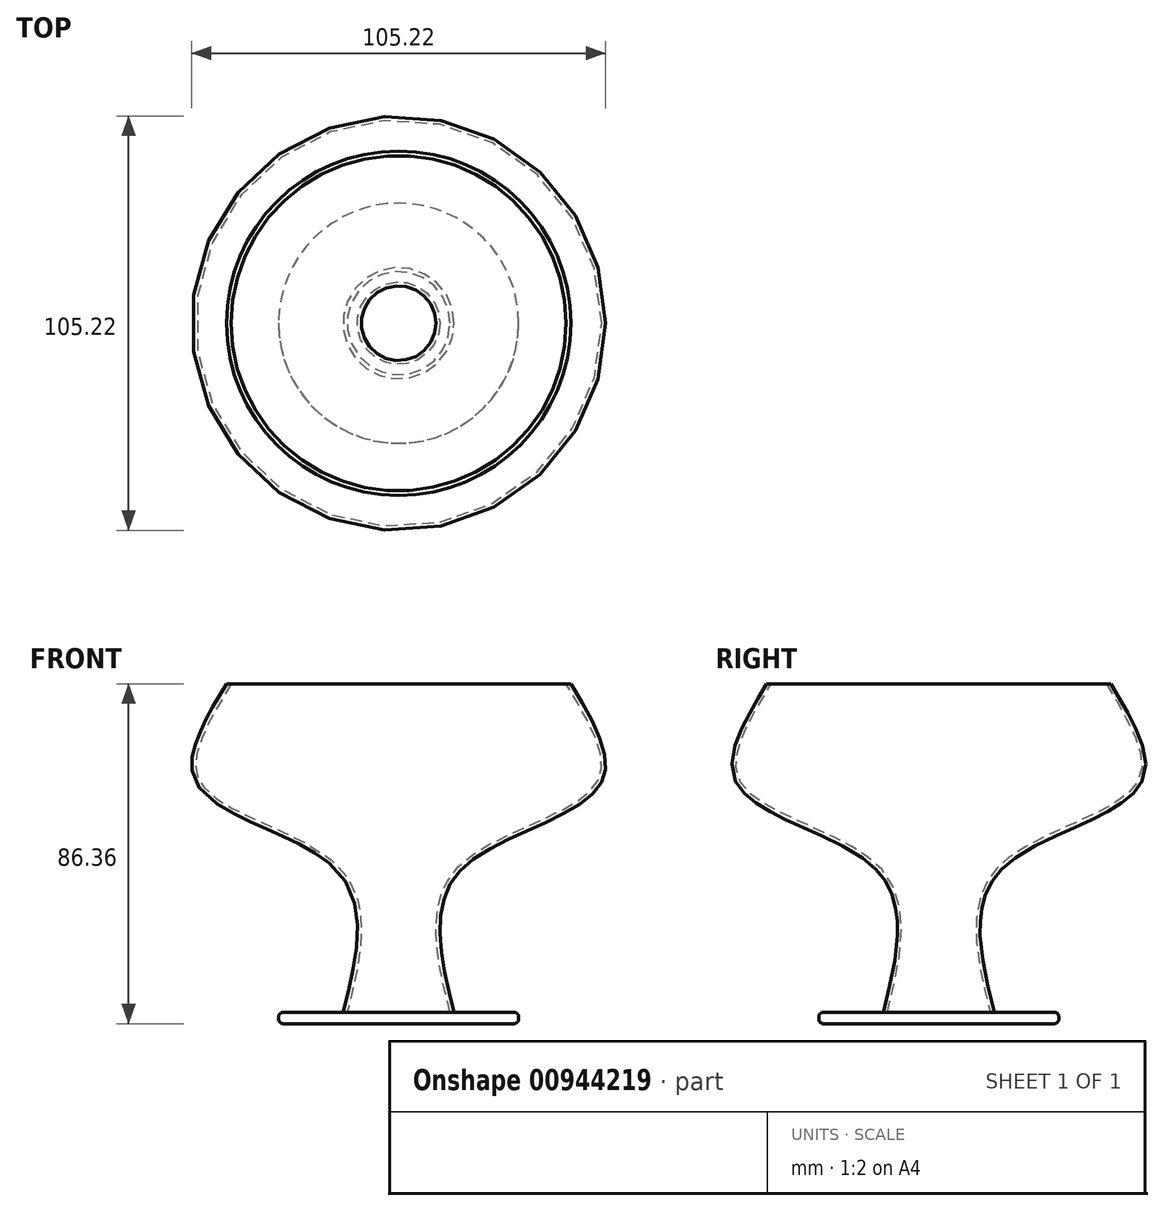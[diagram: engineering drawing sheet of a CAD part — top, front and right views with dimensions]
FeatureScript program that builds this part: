
annotation { "Feature Type Name" : "Feature", "Feature Type Description" : "" }
export const myFeature = defineFeature(function(context is Context, id is Id, definition is map)
    precondition{}
    {
        {
            var Q0;
            Q0=qCreatedBy(makeId("Top.planeOp"),FACE);
            var sketch = newSketch(context, id + "F0", { "sketchPlane" : qUnion([Q0])});
            skCircle(sketch, "E0", {"center": v(0, 0) * mm, "radius": 14.89 * mm});
            skSolve(sketch);
        }
        {
            var Q0;
            Q0=qCreatedBy(makeId("Top.planeOp"),FACE);
            cPlane(context, id + "F1", {"entities" : qUnion([Q0]), "cplaneType" : CPlaneType.OFFSET, "offset" : 86.36 * mm, "width" : 152.4 * mm, "height" : 152.4 * mm});
        }
        {
            var Q0;
            Q0=qCreatedBy(id+"F1.planeOp",FACE);
            var sketch = newSketch(context, id + "F2", { "sketchPlane" : qUnion([Q0])});
            skCircle(sketch, "E1", {"center": v(0, 0) * mm, "radius": 43.74 * mm});
            skSolve(sketch);
        }
        {
            var Q0;
            Q0=qCreatedBy(makeId("Top.planeOp"),FACE);
            cPlane(context, id + "F3", {"entities" : qUnion([Q0]), "cplaneType" : CPlaneType.OFFSET, "offset" : 38.2 * mm, "width" : 150 * mm, "height" : 150 * mm});
        }
        {
            var Q0;
            Q0=qCreatedBy(id+"F3.planeOp",FACE);
            cPlane(context, id + "F4", {"entities" : qUnion([Q0]), "cplaneType" : CPlaneType.OFFSET, "offset" : 25 * mm, "width" : 150 * mm, "height" : 150 * mm});
        }
        {
            var Q0;
            Q0=qCreatedBy(id+"F4.planeOp",FACE);
            var sketch = newSketch(context, id + "F5", { "sketchPlane" : qUnion([Q0])});
            skCircle(sketch, "E2", {"center": v(0, 0) * mm, "radius": 52.3 * mm});
            skSolve(sketch);
        }
        {
            var Q0;
            Q0=qCreatedBy(id+"F3.planeOp",FACE);
            var sketch = newSketch(context, id + "F6", { "sketchPlane" : qUnion([Q0])});
            skCircle(sketch, "E3", {"center": v(0, 0) * mm, "radius": 15 * mm});
            skSolve(sketch);
        }
        {
            var Q0;
            Q0=makeQuery(id+"F0.imprint","IMPRINT",FACE,{"disambiguationData":[TD([[makeQuery(id+"F0.imprint","IMPRINT",EDGE,{"derivedFrom":sQuery(id+"F0.wireOp",EDGE,"E0")}),1.0]])]});
            var Q1;
            Q1=makeQuery(id+"F6.imprint","IMPRINT",FACE,{"disambiguationData":[TD([[makeQuery(id+"F6.imprint","IMPRINT",EDGE,{"derivedFrom":sQuery(id+"F6.wireOp",EDGE,"E3")}),1.0]])]});
            var Q2;
            Q2=makeQuery(id+"F5.imprint","IMPRINT",FACE,{"disambiguationData":[TD([[makeQuery(id+"F5.imprint","IMPRINT",EDGE,{"derivedFrom":sQuery(id+"F5.wireOp",EDGE,"E2")}),1.0]])]});
            var Q3;
            Q3=makeQuery(id+"F2.imprint","IMPRINT",FACE,{"disambiguationData":[TD([[makeQuery(id+"F2.imprint","IMPRINT",EDGE,{"derivedFrom":sQuery(id+"F2.wireOp",EDGE,"E1")}),1.0]])]});
            loft(context, id + "F7", {"sheetProfilesArray" : [{ "sheetProfileEntities" : qUnion([Q0]) }, { "sheetProfileEntities" : qUnion([Q1]) }, { "sheetProfileEntities" : qUnion([Q2]) }, { "sheetProfileEntities" : qUnion([Q3]) }]});
        }
        {
            var Q0;
            Q0=makeQuery(id+"F7.opLoft","CAP_FACE",FACE,{"disambiguationData":[OSD([makeQuery(id+"F2.imprint","IMPRINT",FACE,{"disambiguationData":[TD([[makeQuery(id+"F2.imprint","IMPRINT",EDGE,{"derivedFrom":sQuery(id+"F2.wireOp",EDGE,"E1")}),1.0]])]})])],"isStart":true});
            shell(context, id + "F8", {"entities" : qUnion([Q0]), "thickness" : 1 * mm});
        }
        {
            var Q0;
            Q0=makeQuery(id+"F7.opLoft","CAP_FACE",FACE,{"disambiguationData":[OSD([makeQuery(id+"F0.imprint","IMPRINT",FACE,{"disambiguationData":[TD([[makeQuery(id+"F0.imprint","IMPRINT",EDGE,{"derivedFrom":sQuery(id+"F0.wireOp",EDGE,"E0")}),1.0]])]})])],"isStart":true});
            var sketch = newSketch(context, id + "F9", { "sketchPlane" : qUnion([Q0])});
            skCircle(sketch, "E4", {"center": v(0, 0) * mm, "radius": 30.5 * mm});
            skSolve(sketch);
        }
        {
            var Q0;
            Q0 = qSketchRegion(id + "F9", true);
            extrude(context, id + "F10", {"entities" : qUnion([Q0]), "operationType" : NewBodyOperationType.ADD, "oppositeDirection" : true, "depth" : 2.9 * mm, "offsetDistance" : 25 * mm});
        }
        {
            var Q0;
            Q0=makeQuery(id+"F10.opExtrude","CAP_EDGE",EDGE,{"disambiguationData":[OSD([sQuery(id+"F9.wireOp",EDGE,"E4")])],"isStart":true});
            var Q1;
            Q1=makeQuery(id+"F10.opExtrude","CAP_EDGE",EDGE,{"disambiguationData":[OSD([sQuery(id+"F9.wireOp",EDGE,"E4")])],"isStart":false});
            fillet(context, id + "F11", {"entities" : qUnion([Q0, Q1]), "radius" : 1.2 * mm, "tangentPropagation" : true, "allowEdgeOverflow" : false});
        }
    });
